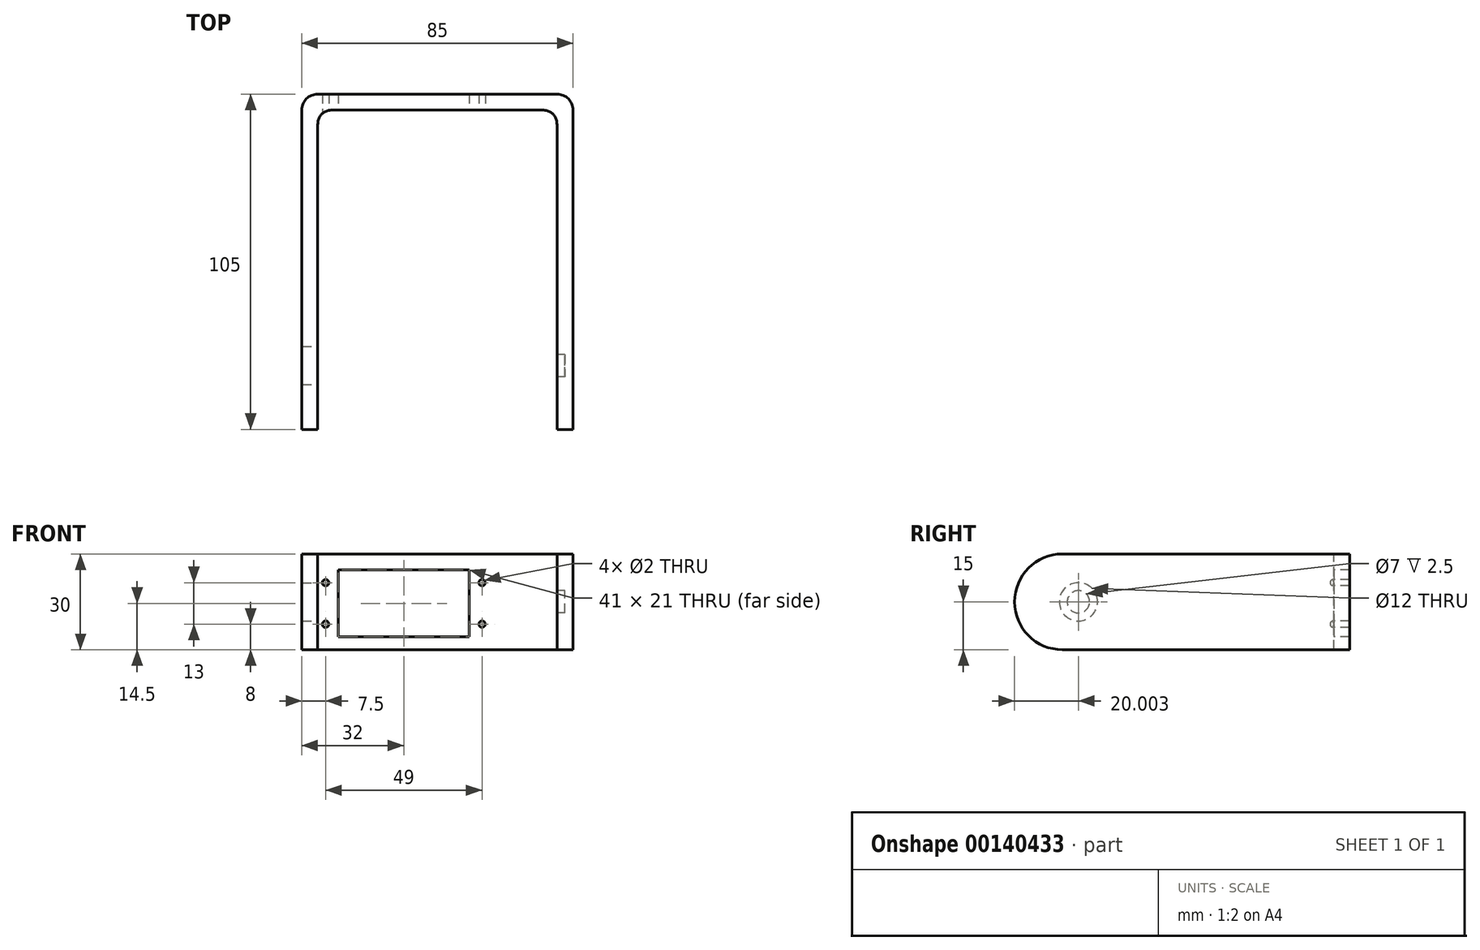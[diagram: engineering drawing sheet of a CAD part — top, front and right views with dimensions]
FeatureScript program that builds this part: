
annotation { "Feature Type Name" : "Feature", "Feature Type Description" : "" }
export const myFeature = defineFeature(function(context is Context, id is Id, definition is map)
    precondition{}
    {
        {
            var Q0;
            Q0=qCreatedBy(makeId("Top.planeOp"),FACE);
            var sketch = newSketch(context, id + "F0", { "sketchPlane" : qUnion([Q0])});
            skLineSegment(sketch, "E0", {"start": v(-37.5, -62.8) * mm, "end": v(-37.5, 37.2) * mm});
            skLineSegment(sketch, "E1", {"start": v(-37.5, 37.2) * mm, "end": v(37.5, 37.2) * mm});
            skLineSegment(sketch, "E2", {"start": v(37.5, 37.2) * mm, "end": v(37.5, -62.8) * mm});
            skLineSegment(sketch, "E3", {"start": v(37.5, -62.8) * mm, "end": v(42.5, -62.8) * mm});
            skLineSegment(sketch, "E4", {"start": v(42.5, -62.8) * mm, "end": v(42.5, 42.2) * mm});
            skLineSegment(sketch, "E5", {"start": v(42.5, 42.2) * mm, "end": v(-42.5, 42.2) * mm});
            skLineSegment(sketch, "E6", {"start": v(-42.5, 42.2) * mm, "end": v(-42.5, -62.8) * mm});
            skLineSegment(sketch, "E7", {"start": v(-42.5, -62.8) * mm, "end": v(-37.5, -62.8) * mm});
            skSolve(sketch);
        }
        {
            var Q0;
            Q0 = qSketchRegion(id + "F0", true);
            extrude(context, id + "F1", {"entities" : qUnion([Q0]), "depth" : 30 * mm});
        }
        {
            var Q0;
            Q0=qCreatedBy(makeId("Right.planeOp"),FACE);
            var sketch = newSketch(context, id + "F2", { "sketchPlane" : qUnion([Q0])});
            skCircle(sketch, "E8", {"center": v(-42.8, 15) * mm, "radius": 3.5 * mm});
            skSolve(sketch);
        }
        {
            var Q0;
            Q0 = qSketchRegion(id + "F2", true);
            extrude(context, id + "F3", {"entities" : qUnion([Q0]), "operationType" : NewBodyOperationType.REMOVE, "depth" : 40 * mm, "hasSecondDirection" : true, "secondDirectionOppositeDirection" : false, "secondDirectionDepth" : 37.5 * mm});
        }
        {
            var Q0;
            Q0=qCreatedBy(makeId("Right.planeOp"),FACE);
            var sketch = newSketch(context, id + "F4", { "sketchPlane" : qUnion([Q0])});
            skCircle(sketch, "E9", {"center": v(-42.8, 15) * mm, "radius": 6 * mm});
            skSolve(sketch);
        }
        {
            var Q0;
            Q0 = qSketchRegion(id + "F4", true);
            extrude(context, id + "F5", {"entities" : qUnion([Q0]), "operationType" : NewBodyOperationType.REMOVE, "oppositeDirection" : true, "depth" : 42.5 * mm, "hasSecondDirection" : true, "secondDirectionOppositeDirection" : true, "secondDirectionDepth" : 37.5 * mm});
        }
        {
            var Q0;
            Q0=makeQuery(id+"F1.opExtrude","CAP_EDGE",EDGE,{"disambiguationData":[OSD([sQuery(id+"F0.wireOp",EDGE,"E3")])],"isStart":false});
            var Q1;
            Q1=makeQuery(id+"F1.opExtrude","CAP_EDGE",EDGE,{"disambiguationData":[OSD([sQuery(id+"F0.wireOp",EDGE,"E3")])],"isStart":true});
            var Q2;
            Q2=makeQuery(id+"F1.opExtrude","CAP_EDGE",EDGE,{"disambiguationData":[OSD([sQuery(id+"F0.wireOp",EDGE,"E7")])],"isStart":false});
            var Q3;
            Q3=makeQuery(id+"F1.opExtrude","CAP_EDGE",EDGE,{"disambiguationData":[OSD([sQuery(id+"F0.wireOp",EDGE,"E7")])],"isStart":true});
            fillet(context, id + "F6", {"entities" : qUnion([Q0, Q1, Q2, Q3]), "radius" : 15 * mm, "tangentPropagation" : true, "allowEdgeOverflow" : false});
        }
        {
            var Q0;
            Q0=makeQuery(id+"F1.opExtrude","SWEPT_EDGE",EDGE,{"disambiguationData":[OSD([sQuery(id+"F0.wireOp",EDGE,"E5"),sQuery(id+"F0.wireOp",EDGE,"E6")])]});
            var Q1;
            Q1=makeQuery(id+"F1.opExtrude","SWEPT_EDGE",EDGE,{"disambiguationData":[OSD([sQuery(id+"F0.wireOp",EDGE,"E4"),sQuery(id+"F0.wireOp",EDGE,"E5")])]});
            fillet(context, id + "F7", {"entities" : qUnion([Q0, Q1]), "radius" : 5 * mm, "tangentPropagation" : true, "allowEdgeOverflow" : false});
        }
        {
            var Q0;
            Q0=makeQuery(id+"F1.opExtrude","SWEPT_EDGE",EDGE,{"disambiguationData":[OSD([sQuery(id+"F0.wireOp",EDGE,"E0"),sQuery(id+"F0.wireOp",EDGE,"E1")])]});
            var Q1;
            Q1=makeQuery(id+"F1.opExtrude","SWEPT_EDGE",EDGE,{"disambiguationData":[OSD([sQuery(id+"F0.wireOp",EDGE,"E1"),sQuery(id+"F0.wireOp",EDGE,"E2")])]});
            fillet(context, id + "F8", {"entities" : qUnion([Q0, Q1]), "radius" : 5 * mm, "tangentPropagation" : true, "rho" : 0.5, "crossSection" : FilletCrossSection.CONIC, "allowEdgeOverflow" : false});
        }
        {
            var Q0;
            Q0=qCreatedBy(makeId("Front.planeOp"),FACE);
            var sketch = newSketch(context, id + "F9", { "sketchPlane" : qUnion([Q0])});
            skLineSegment(sketch, "E10.bottom", {"start": v(-31, 4) * mm, "end": v(10, 4) * mm});
            skLineSegment(sketch, "E10.top", {"start": v(-31, 25) * mm, "end": v(10, 25) * mm});
            skLineSegment(sketch, "E10.left", {"start": v(-31, 4) * mm, "end": v(-31, 25) * mm});
            skLineSegment(sketch, "E10.right", {"start": v(10, 4) * mm, "end": v(10, 25) * mm});
            skSolve(sketch);
        }
        {
            var Q0;
            Q0 = qSketchRegion(id + "F9", true);
            extrude(context, id + "F10", {"entities" : qUnion([Q0]), "operationType" : NewBodyOperationType.REMOVE, "oppositeDirection" : true, "depth" : 45 * mm, "hasSecondDirection" : true, "secondDirectionOppositeDirection" : true, "secondDirectionDepth" : 33 * mm});
        }
        {
            var Q0;
            Q0=qCreatedBy(makeId("Front.planeOp"),FACE);
            var sketch = newSketch(context, id + "F11", { "sketchPlane" : qUnion([Q0])});
            skCircle(sketch, "E11", {"center": v(14, 21) * mm, "radius": 1 * mm});
            skCircle(sketch, "E12", {"center": v(14, 8) * mm, "radius": 1 * mm});
            skCircle(sketch, "E13", {"center": v(-35, 21) * mm, "radius": 1 * mm});
            skCircle(sketch, "E14", {"center": v(-35, 8) * mm, "radius": 1 * mm});
            skSolve(sketch);
        }
        {
            var Q0;
            Q0 = qSketchRegion(id + "F11", true);
            extrude(context, id + "F12", {"entities" : qUnion([Q0]), "operationType" : NewBodyOperationType.REMOVE, "oppositeDirection" : true, "depth" : 45 * mm, "hasSecondDirection" : true, "secondDirectionOppositeDirection" : true, "secondDirectionDepth" : 35 * mm});
        }
    });
